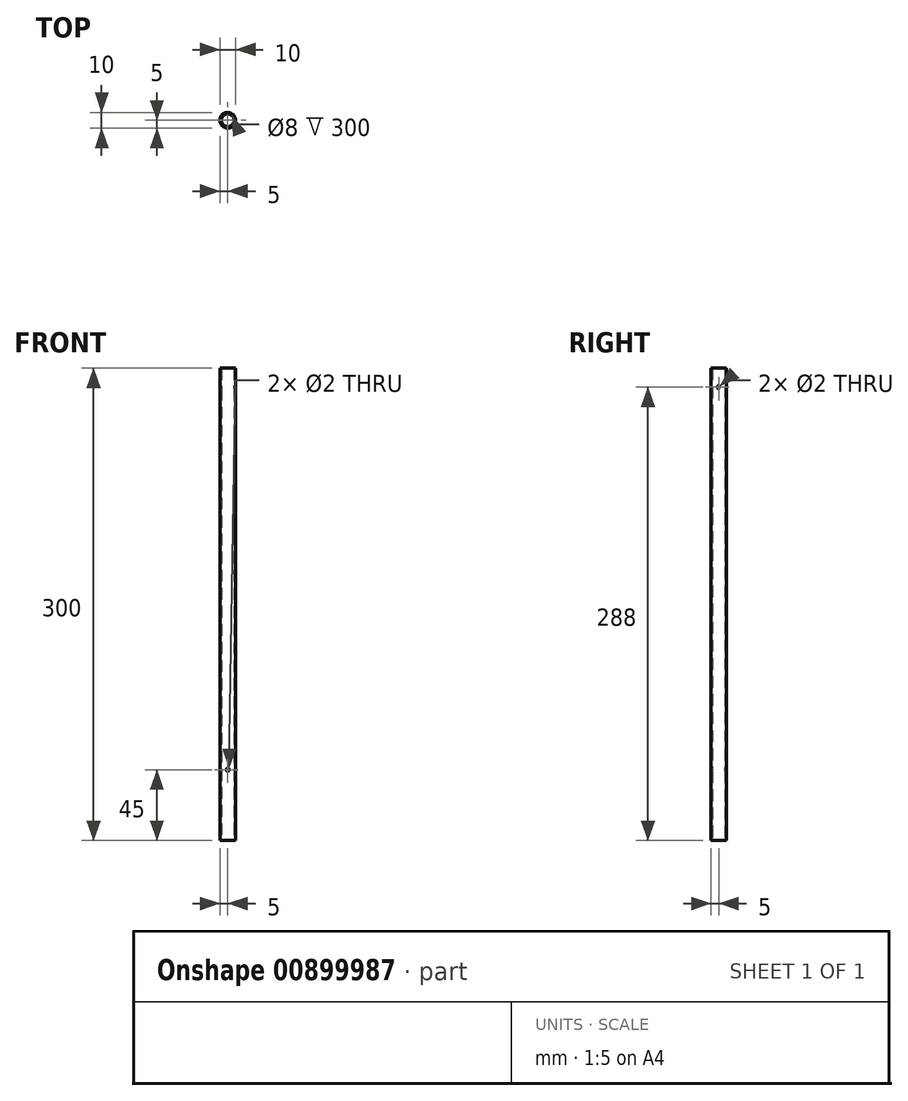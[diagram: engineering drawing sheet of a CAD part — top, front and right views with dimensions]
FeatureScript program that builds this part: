
annotation { "Feature Type Name" : "Feature", "Feature Type Description" : "" }
export const myFeature = defineFeature(function(context is Context, id is Id, definition is map)
    precondition{}
    {
        {
            var Q0;
            Q0=qCreatedBy(makeId("Top.planeOp"),FACE);
            var sketch = newSketch(context, id + "F0", { "sketchPlane" : qUnion([Q0])});
            skCircle(sketch, "E0", {"center": v(0, 0) * mm, "radius": 4 * mm});
            skCircle(sketch, "E1", {"center": v(0, 0) * mm, "radius": 5 * mm});
            skSolve(sketch);
        }
        {
            var Q0;
            Q0=qSketchRegion(id+"F0",true);
            extrude(context, id + "F1", {"entities" : qUnion([Q0]), "endBound" : BoundingType.SYMMETRIC, "depth" : 300 * mm, "offsetDistance" : 25 * mm});
        }
        {
            var Q0;
            Q0=qCreatedBy(makeId("Front.planeOp"),FACE);
            var sketch = newSketch(context, id + "F2", { "sketchPlane" : qUnion([Q0])});
            skCircle(sketch, "E2", {"center": v(0, -105) * mm, "radius": 1 * mm});
            skSolve(sketch);
        }
        {
            var Q0;
            Q0 = qSketchRegion(id + "F2", true);
            extrude(context, id + "F3", {"entities" : qUnion([Q0]), "operationType" : NewBodyOperationType.REMOVE, "endBound" : BoundingType.THROUGH_ALL, "oppositeDirection" : true, "depth" : 25 * mm, "offsetDistance" : 25 * mm, "hasSecondDirection" : true, "secondDirectionBound" : SecondDirectionBoundingType.THROUGH_ALL, "secondDirectionOppositeDirection" : false, "secondDirectionDepth" : 25 * mm});
        }
        {
            var Q0;
            Q0=qCreatedBy(makeId("Right.planeOp"),FACE);
            var sketch = newSketch(context, id + "F4", { "sketchPlane" : qUnion([Q0])});
            skCircle(sketch, "E3", {"center": v(0, 138) * mm, "radius": 1 * mm});
            skSolve(sketch);
        }
        {
            var Q0;
            Q0 = qSketchRegion(id + "F4", true);
            extrude(context, id + "F5", {"entities" : qUnion([Q0]), "operationType" : NewBodyOperationType.REMOVE, "endBound" : BoundingType.THROUGH_ALL, "oppositeDirection" : true, "depth" : 25 * mm, "offsetDistance" : 25 * mm, "hasSecondDirection" : true, "secondDirectionBound" : SecondDirectionBoundingType.THROUGH_ALL, "secondDirectionOppositeDirection" : false, "secondDirectionDepth" : 25 * mm});
        }
    });
